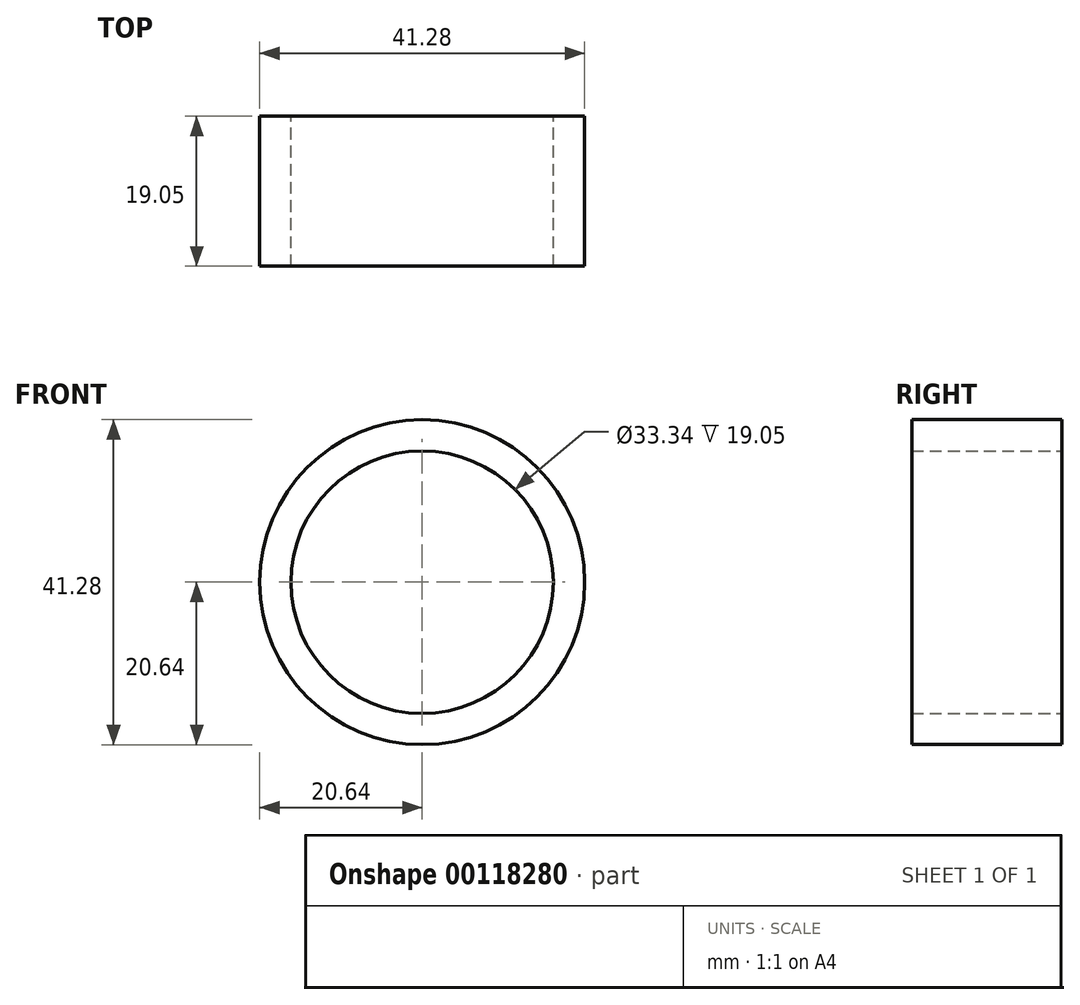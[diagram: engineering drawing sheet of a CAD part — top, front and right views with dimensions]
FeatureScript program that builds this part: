
annotation { "Feature Type Name" : "Feature", "Feature Type Description" : "" }
export const myFeature = defineFeature(function(context is Context, id is Id, definition is map)
    precondition{}
    {
        {
            var Q0;
            Q0=qCreatedBy(makeId("Front.planeOp"),FACE);
            var sketch = newSketch(context, id + "F0", { "sketchPlane" : qUnion([Q0])});
            skCircle(sketch, "E0", {"center": v(0, 0) * mm, "radius": 20.64 * mm});
            skCircle(sketch, "E1", {"center": v(0, 0) * mm, "radius": 16.67 * mm});
            skSolve(sketch);
        }
        {
            var Q0;
            Q0=makeQuery(id+"F0.imprint","IMPRINT",FACE,{"disambiguationData":[TD([[makeQuery(id+"F0.imprint","IMPRINT",EDGE,{"derivedFrom":sQuery(id+"F0.wireOp",EDGE,"E0")}),1.0]])]});
            extrude(context, id + "F1", {"entities" : qUnion([Q0]), "depth" : 19.05 * mm});
        }
    });
